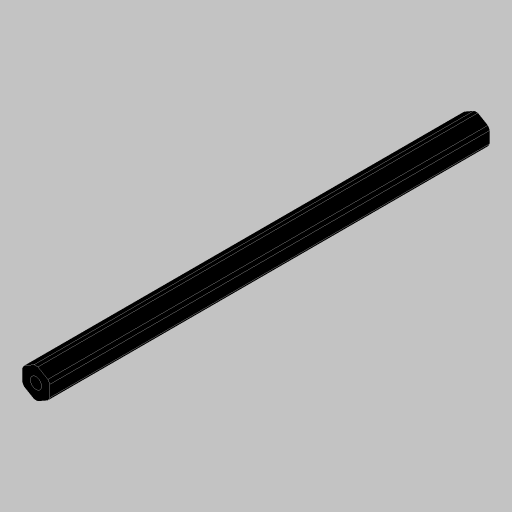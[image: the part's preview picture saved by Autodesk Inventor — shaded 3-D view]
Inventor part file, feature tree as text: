
AUTODESK INVENTOR PART (.ipt)
format: ipt  version: 2023.5 (Build 275446000, 446)  size: 119,296 bytes
history: native  units: in
note: dims shown in document units (in); Inventor stores cm internally (conversion verified against a paired STEP export)
features: extrude x2, projected_geometry x2, hole x1
ambient origin geometry x8: Origin, YZ Plane, XZ Plane, XY Plane, X Axis, Y Axis, Z Axis, Center Point
bodies: Solid1 (feature_tree)
feature tree (5):
  extrude  "Extrusion1"  TaperAngle=0.0deg  [1 undecoded]
  hole  "Hole1"  [1 undecoded]
  extrude  "Extrusion3"  TaperAngle=0.0deg  [1 undecoded]
  projected_geometry  "Project Cut Edges1"
  projected_geometry  "Project Cut Edges2"
note: 3 required parameter values undecoded (feature->parameter linkage not recoverable at this tier; creation-order binding heuristic only, values carry confidence <= 0.55)
